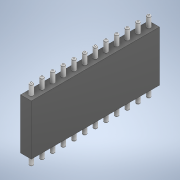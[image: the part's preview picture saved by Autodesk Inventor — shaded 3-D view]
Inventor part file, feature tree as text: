
AUTODESK INVENTOR PART (.ipt)
format: ipt  version: 2021 (Build 250183000, 183)  size: 156,160 bytes
history: native  units: in
note: dims shown in document units (in); Inventor stores cm internally (conversion verified against a paired STEP export)
features: extrude x2, sketch x2, fillet x1, pattern_linear x1, plane x1, mirror x1
ambient origin geometry x8: Origin, YZ Plane, XZ Plane, XY Plane, X Axis, Y Axis, Z Axis, Center Point
bodies: Solid1 (feature_tree)
feature tree (8):
  extrude  "Extrusion1"  Depth=0.1in
  extrude  "Extrusion2"  Depth=0.1in
  fillet  "Fillet1"  Radius=0.05in
  pattern_linear  "Rectangular Pattern1"  Spacing1=0.05in  [1 undecoded]
  plane  "Work Plane1"
  mirror  "Mirror1"
  sketch  "Sketch1"  dims[d0=1.2in d1=0.1in]
  sketch  "Sketch2"  dims[d2=0.4724in d3=0.0in d4=0.0354in d5=0.05in d6=0.05in d7=0.1in d8=0.0in d9=0.01in d10=4.7244in d12=0.1in]
note: 1 required parameter value undecoded (feature->parameter linkage not recoverable at this tier; creation-order binding heuristic only, values carry confidence <= 0.55)
